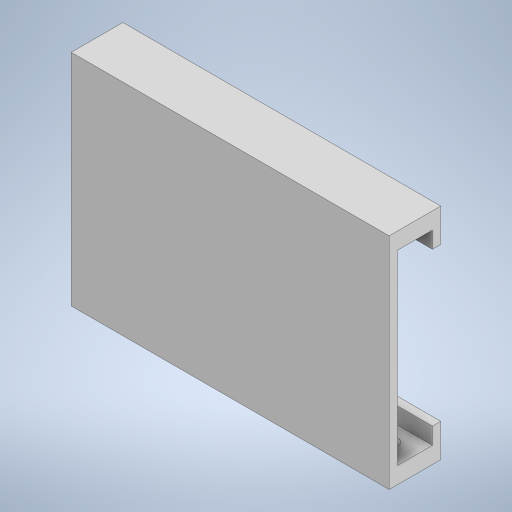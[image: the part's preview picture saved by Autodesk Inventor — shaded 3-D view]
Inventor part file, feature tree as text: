
AUTODESK INVENTOR PART (.ipt)
format: ipt  version: 2024 (Build 280153000, 153)  size: 287,232 bytes
history: native  units: mm
features: extrude x4, sketch x4, mirror x1
ambient origin geometry x8: Origin, YZ Plane, XZ Plane, XY Plane, X Axis, Y Axis, Z Axis, Center Point
bodies: Volumenkörper1 (feature_tree)
feature tree (9):
  extrude  "Extrusion1"  Depth=22.4mm
  extrude  "Extrusion2"  Depth=2.0mm
  extrude  "Extrusion3"  Depth=5.2mm TaperAngle=0.0deg
  extrude  "Extrusion4"  Depth=2.0mm
  mirror  "Spiegeln1"
  sketch  "Skizze1"  dims[d0=36.2mm d1=22.4mm]
  sketch  "Skizze2"  dims[d2=1.0mm d3=0.0mm d4=2.0mm]
  sketch  "Skizze3"  dims[d5=2.0mm d6=5.2mm d7=0.0mm]
  sketch  "Skizze4"  dims[d8=2.0mm d9=2.0mm d10=2.0mm d11=1.0mm d12=0.0mm d13=1.5mm d14=2.0mm d15=0.3mm d16=-8.726646mm]
